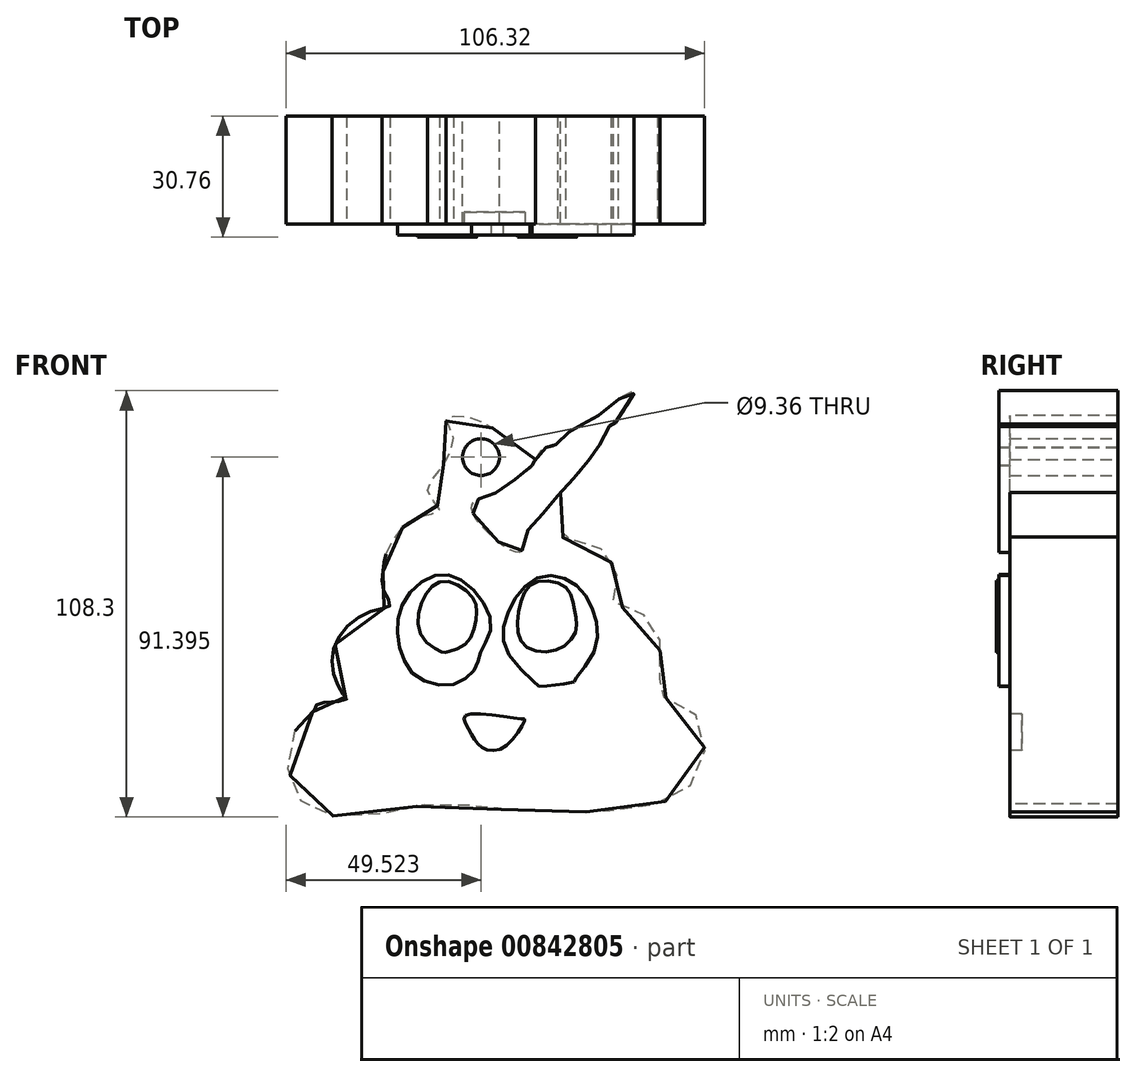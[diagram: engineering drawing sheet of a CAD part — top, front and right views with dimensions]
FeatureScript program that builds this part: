
annotation { "Feature Type Name" : "Feature", "Feature Type Description" : "" }
export const myFeature = defineFeature(function(context is Context, id is Id, definition is map)
    precondition{}
    {
        {
            var Q0;
            Q0=qCreatedBy(makeId("Front.planeOp"),FACE);
            var sketch = newSketch(context, id + "F0", { "sketchPlane" : qUnion([Q0])});
            skFitSpline(sketch, "E0", {"points": [v(-50.2, -59.04) * mm, v(-51.34, -47.64) * mm, v(-44.5, -39.36) * mm, v(-44.21, -38.5) * mm, v(-36.8, -37.37) * mm, v(-37.37, -36.23) * mm, v(-40.22, -29.67) * mm, v(-38.5, -21.1) * mm, v(-30.24, -14.83) * mm, v(-25.67, -13.4) * mm, v(-27.38, -9.41) * mm, v(-27.38, -4.28) * mm, v(-26.53, 0) * mm, v(-22.82, 6) * mm, v(-18.26, 9.13) * mm, v(-13.12, 10.84) * mm, v(-15.97, 15.12) * mm, v(-14.26, 19.4) * mm, v(-10.84, 24.53) * mm, v(-9.7, 29.95) * mm, v(-11.4, 33.66) * mm, v(-7.99, 34.8) * mm, v(0, 31.95) * mm, v(6.28, 27.38) * mm, v(10.84, 23.96) * mm, v(18.83, 11.4) * mm, v(17.11, 4) * mm, v(16.83, 4) * mm, v(25.39, 2.28) * mm, v(28.8, 0) * mm, v(32.23, -7.99) * mm, v(31.1, -12.55) * mm, v(39.65, -16.26) * mm, v(42.79, -23.1) * mm, v(42.5, -33.94) * mm, v(42.5, -35.94) * mm, v(50.49, -39.65) * mm, v(54.2, -49.92) * mm, v(49.63, -60.19) * mm, v(36.51, -65.03) * mm, v(20.82, -65.9) * mm, v(3.42, -65.32) * mm, v(-14.55, -63.9) * mm, v(-29.95, -66.75) * mm, v(-45.92, -65.32) * mm, v(-50.2, -59.04) * mm]});
            skSolve(sketch);
        }
        {
            var Q0;
            Q0=makeQuery(id+"F0.imprint","IMPRINT",FACE,{"disambiguationData":[TD([[makeQuery(id+"F0.imprint","IMPRINT",EDGE,{"derivedFrom":sQuery(id+"F0.wireOp",EDGE,"E0")}),-1.0]])]});
            extrude(context, id + "F1", {"entities" : qUnion([Q0]), "depth" : 27.43 * mm, "offsetDistance" : 25.4 * mm});
        }
        {
            var Q0;
            Q0=qCreatedBy(makeId("Front.planeOp"),FACE);
            var sketch = newSketch(context, id + "F2", { "sketchPlane" : qUnion([Q0])});
            skFitSpline(sketch, "E1", {"points": [v(-4.6, 9.93) * mm, v(-3.83, 13.3) * mm, v(0, 14.62) * mm, v(5.4, 18.12) * mm, v(10.42, 22.08) * mm, v(9.86, 21.96) * mm, v(10.59, 22.7) * mm, v(13.31, 26.47) * mm, v(15.33, 26.6) * mm, v(16.34, 27.39) * mm, v(19.52, 30.38) * mm, v(21.8, 32.02) * mm, v(25.56, 33.67) * mm, v(30.86, 37.69) * mm, v(36.34, 40.86) * mm, v(30.56, 32.09) * mm, v(30.45, 32.65) * mm, v(28.56, 29.05) * mm, v(26.12, 25.34) * mm, v(22.22, 20.16) * mm, v(17.2, 14.75) * mm, v(12.75, 9.45) * mm, v(8.8, 4.55) * mm, v(7.1, 0) * mm, v(-4.6, 9.93) * mm]});
            skSolve(sketch);
        }
        {
            var Q0;
            Q0=makeQuery(id+"F2.imprint","IMPRINT",FACE,{"disambiguationData":[TD([[makeQuery(id+"F2.imprint","IMPRINT",EDGE,{"derivedFrom":sQuery(id+"F2.wireOp",EDGE,"E1")}),-1.0]])]});
            extrude(context, id + "F3", {"entities" : qUnion([Q0]), "operationType" : NewBodyOperationType.ADD, "depth" : 30.23 * mm, "offsetDistance" : 25.4 * mm});
        }
        {
            var Q0;
            Q0=makeQuery(id+"F1.opExtrude","CAP_FACE",FACE,{"disambiguationData":[OSD([sQuery(id+"F0.wireOp",EDGE,"E0")])],"isStart":false});
            var sketch = newSketch(context, id + "F4", { "sketchPlane" : qUnion([Q0])});
            skFitSpline(sketch, "E2", {"points": [v(-6.56, -41.36) * mm, v(7.7, -42.22) * mm, v(8.56, -42.5) * mm, v(3.42, -49.35) * mm, v(-2.57, -49.35) * mm, v(-5.7, -44.78) * mm, v(-6.56, -41.36) * mm]});
            skSolve(sketch);
        }
        {
            var Q0;
            Q0=makeQuery(id+"F4.imprint","IMPRINT",FACE,{"disambiguationData":[TD([[makeQuery(id+"F4.imprint","IMPRINT",EDGE,{"derivedFrom":sQuery(id+"F4.wireOp",EDGE,"E2")}),-1.0]])]});
            extrude(context, id + "F5", {"entities" : qUnion([Q0]), "operationType" : NewBodyOperationType.REMOVE, "oppositeDirection" : true, "depth" : 3.05 * mm, "offsetDistance" : 25.4 * mm});
        }
        {
            var Q0;
            Q0=qCreatedBy(makeId("Front.planeOp"),FACE);
            var sketch = newSketch(context, id + "F6", { "sketchPlane" : qUnion([Q0])});
            skFitSpline(sketch, "E3", {"points": [v(26.07, -25.21) * mm, v(25.83, -14.58) * mm, v(20.16, -7.24) * mm, v(11, -6.79) * mm, v(4.06, -15.94) * mm, v(4.36, -25.66) * mm, v(12.16, -33.9) * mm, v(12.42, -34.01) * mm, v(20.97, -32.97) * mm, v(21.08, -32.7) * mm, v(26.07, -25.21) * mm]});
            skFitSpline(sketch, "E4", {"points": [v(-9.49, -33.45) * mm, v(-4, -29.26) * mm, v(-2.62, -25.21) * mm, v(0, -18.32) * mm, v(-5.6, -8.46) * mm, v(-14.16, -5.79) * mm, v(-22.4, -12.84) * mm, v(-23.54, -22.27) * mm, v(-19.43, -31.12) * mm, v(-9.49, -33.45) * mm]});
            skSolve(sketch);
        }
        {
            var Q0;
            Q0=makeQuery(id+"F6.imprint","IMPRINT",FACE,{"disambiguationData":[TD([[makeQuery(id+"F6.imprint","IMPRINT",EDGE,{"derivedFrom":sQuery(id+"F6.wireOp",EDGE,"E3")}),1.0]])]});
            var Q1;
            Q1=makeQuery(id+"F6.imprint","IMPRINT",FACE,{"disambiguationData":[TD([[makeQuery(id+"F6.imprint","IMPRINT",EDGE,{"derivedFrom":sQuery(id+"F6.wireOp",EDGE,"E4")}),1.0]])]});
            extrude(context, id + "F7", {"entities" : qUnion([Q0, Q1]), "operationType" : NewBodyOperationType.ADD, "depth" : 30.23 * mm, "offsetDistance" : 25.4 * mm});
        }
        {
            var Q0;
            Q0=qCreatedBy(makeId("Front.planeOp"),FACE);
            var sketch = newSketch(context, id + "F8", { "sketchPlane" : qUnion([Q0])});
            skFitSpline(sketch, "E5", {"points": [v(21.15, -14.55) * mm, v(21.5, -19.97) * mm, v(16.34, -24.84) * mm, v(8.18, -23.3) * mm, v(7.05, -14.79) * mm, v(10.9, -7.7) * mm, v(19.05, -8.94) * mm, v(21.15, -14.55) * mm]});
            skFitSpline(sketch, "E6", {"points": [v(-4.7, -11.45) * mm, v(-3.78, -16.55) * mm, v(-6.51, -23.3) * mm, v(-11.57, -25.3) * mm, v(-12.14, -25.33) * mm, v(-17.58, -21.35) * mm, v(-17.34, -11.9) * mm, v(-11.88, -7.28) * mm, v(-4.7, -11.45) * mm]});
            skSolve(sketch);
        }
        {
            var Q0;
            Q0=makeQuery(id+"F8.imprint","IMPRINT",FACE,{"disambiguationData":[TD([[makeQuery(id+"F8.imprint","IMPRINT",EDGE,{"derivedFrom":sQuery(id+"F8.wireOp",EDGE,"E6")}),-1.0]])]});
            var Q1;
            Q1=makeQuery(id+"F8.imprint","IMPRINT",FACE,{"disambiguationData":[TD([[makeQuery(id+"F8.imprint","IMPRINT",EDGE,{"derivedFrom":sQuery(id+"F8.wireOp",EDGE,"E5")}),-1.0]])]});
            extrude(context, id + "F9", {"entities" : qUnion([Q0, Q1]), "operationType" : NewBodyOperationType.ADD, "depth" : 30.76 * mm, "offsetDistance" : 25.4 * mm});
        }
        {
            var Q0;
            Q0=qCreatedBy(makeId("Front.planeOp"),FACE);
            var sketch = newSketch(context, id + "F10", { "sketchPlane" : qUnion([Q0])});
            skCircle(sketch, "E7", {"center": v(-2.57, 24.25) * mm, "radius": 4.68 * mm});
            skSolve(sketch);
        }
        {
            var Q0;
            Q0=makeQuery(id+"F10.imprint","IMPRINT",FACE,{"disambiguationData":[TD([[makeQuery(id+"F10.imprint","IMPRINT",EDGE,{"derivedFrom":sQuery(id+"F10.wireOp",EDGE,"E7")}),1.0]])]});
            extrude(context, id + "F11", {"entities" : qUnion([Q0]), "operationType" : NewBodyOperationType.REMOVE, "depth" : 48.77 * mm, "offsetDistance" : 25.4 * mm});
        }
    });
